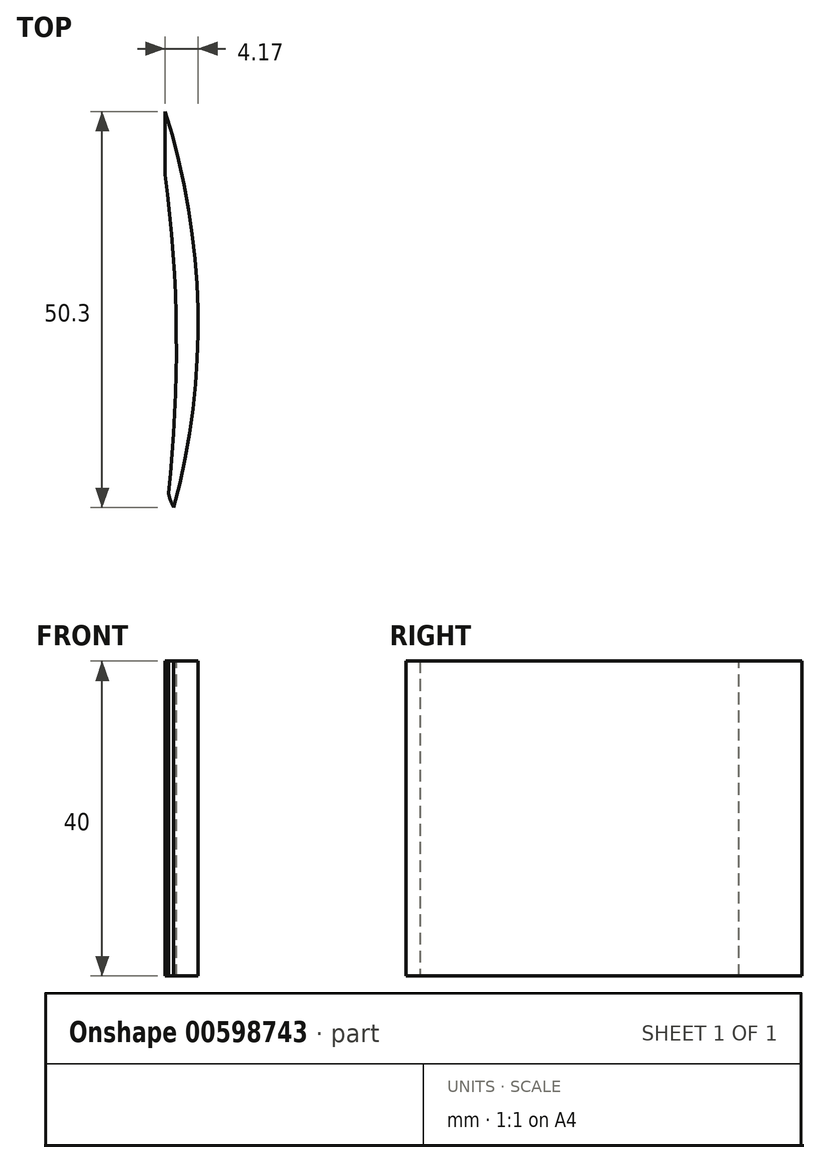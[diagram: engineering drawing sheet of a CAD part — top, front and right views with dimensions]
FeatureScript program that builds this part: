
annotation { "Feature Type Name" : "Feature", "Feature Type Description" : "" }
export const myFeature = defineFeature(function(context is Context, id is Id, definition is map)
    precondition{}
    {
        {
            var Q0;
            Q0=qCreatedBy(makeId("Top.planeOp"),FACE);
            var sketch = newSketch(context, id + "F0", { "sketchPlane" : qUnion([Q0])});
            skLineSegment(sketch, "E0.bottom", {"start": v(-2.5, 27) * mm, "end": v(2.5, 27) * mm});
            skLineSegment(sketch, "E0.top", {"start": v(-2.5, -27) * mm, "end": v(2.5, -27) * mm});
            skLineSegment(sketch, "E0.left", {"start": v(-2.5, 27) * mm, "end": v(-2.5, -27) * mm});
            skLineSegment(sketch, "E0.right", {"start": v(2.5, 27) * mm, "end": v(2.5, -27) * mm});
            skPoint(sketch, "E0.middle", {"position": v(0, 0) * mm});
            skSolve(sketch);
        }
        {
            var Q0;
            Q0=makeQuery(id+"F0.imprint","IMPRINT",FACE,{"disambiguationData":[TD([[makeQuery(id+"F0.imprint","IMPRINT",EDGE,{"derivedFrom":sQuery(id+"F0.wireOp",EDGE,"E0.bottom")}),-1.0]])]});
            extrude(context, id + "F1", {"entities" : qUnion([Q0]), "depth" : 40 * mm, "offsetDistance" : 25.4 * mm});
        }
        {
            var Q0;
            Q0=makeQuery(id+"F1.opExtrude","CAP_FACE",FACE,{"disambiguationData":[OSD([sQuery(id+"F0.wireOp",EDGE,"E0.bottom"),sQuery(id+"F0.wireOp",EDGE,"E0.top"),sQuery(id+"F0.wireOp",EDGE,"E0.left"),sQuery(id+"F0.wireOp",EDGE,"E0.right")])],"isStart":false});
            var sketch = newSketch(context, id + "F2", { "sketchPlane" : qUnion([Q0])});
            skLineSegment(sketch, "E1", {"start": v(-2.5, 27) * mm, "end": v(-2.5, 19) * mm});
            skLineSegment(sketch, "E2", {"start": v(-2.5, 19) * mm, "end": v(-2.5, -25) * mm});
            skArc(sketch, "E3", {"start": v(-2.5, -25) * mm, "mid": v(-1.09, -3) * mm, "end": v(-2.5, 19) * mm});
            skArc(sketch, "E4", {"start": v(-2.5, -27) * mm, "mid": v(1.67, 0) * mm, "end": v(-2.5, 27) * mm});
            skLineSegment(sketch, "E5", {"start": v(-2.5, -27) * mm, "end": v(-1.5, -27) * mm});
            skArc(sketch, "E6", {"start": v(-1.75, -18.1) * mm, "mid": v(-2.18, -20.73) * mm, "end": v(-1.42, -23.3) * mm});
            skSolve(sketch);
        }
        {
            var Q0;
            {var subQ0=sQuery(id+"F2.wireOp",EDGE,"E2");Q0=makeQuery(id+"F2.imprint","IMPRINT",FACE,{"disambiguationData":[TD([[makeQuery(id+"F2.imprint","IMPRINT",EDGE,{"derivedFrom":subQ0}),1.0]])]});}
            extrude(context, id + "F3", {"entities" : qUnion([Q0]), "operationType" : NewBodyOperationType.REMOVE, "oppositeDirection" : true, "depth" : 40 * mm, "offsetDistance" : 25.4 * mm});
        }
        {
            var Q0;
            {var subQ1=sQuery(id+"F2.wireOp",EDGE,"E1");Q0=makeQuery(id+"F2.imprint","IMPRINT",FACE,{"disambiguationData":[TD([[makeQuery(id+"F2.imprint","IMPRINT",EDGE,{"derivedFrom":subQ1}),1.0]])]});}
            extrude(context, id + "F4", {"entities" : qUnion([Q0]), "operationType" : NewBodyOperationType.ADD, "depth" : 40 * mm, "offsetDistance" : 25.4 * mm});
        }
        {
            var Q0;
            Q0=makeQuery(id+"F1.opExtrude","CAP_FACE",FACE,{"disambiguationData":[OSD([sQuery(id+"F0.wireOp",EDGE,"E0.bottom"),sQuery(id+"F0.wireOp",EDGE,"E0.top"),sQuery(id+"F0.wireOp",EDGE,"E0.left"),sQuery(id+"F0.wireOp",EDGE,"E0.right")])],"isStart":true});
            extrude(context, id + "F5", {"entities" : qUnion([Q0]), "operationType" : NewBodyOperationType.REMOVE, "oppositeDirection" : true, "depth" : 40 * mm, "offsetDistance" : 25.4 * mm});
        }
    });
